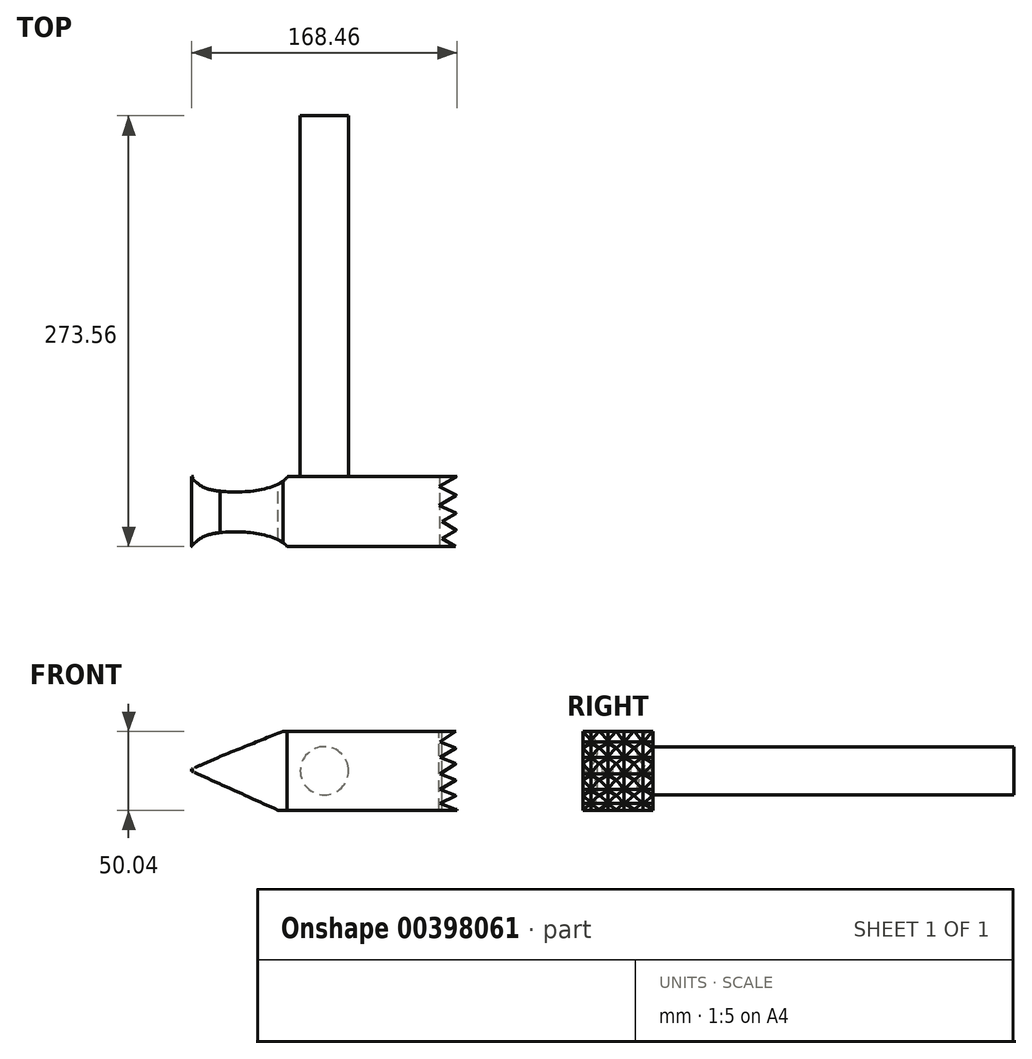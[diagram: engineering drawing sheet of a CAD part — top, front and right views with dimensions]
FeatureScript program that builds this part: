
annotation { "Feature Type Name" : "Feature", "Feature Type Description" : "" }
export const myFeature = defineFeature(function(context is Context, id is Id, definition is map)
    precondition{}
    {
        {
            var Q0;
            Q0=qCreatedBy(makeId("Front.planeOp"),FACE);
            var sketch = newSketch(context, id + "F0", { "sketchPlane" : qUnion([Q0])});
            skCircle(sketch, "E0", {"center": v(0, 0) * mm, "radius": 15.3 * mm});
            skSolve(sketch);
        }
        {
            var Q0;
            Q0 = qSketchRegion(id + "F0", true);
            extrude(context, id + "F1", {"entities" : qUnion([Q0]), "depth" : 229.1 * mm});
        }
        {
            var Q0;
            Q0=makeQuery(id+"F1.opExtrude","CAP_FACE",FACE,{"disambiguationData":[OSD([sQuery(id+"F0.wireOp",EDGE,"E0")])],"isStart":false});
            var sketch = newSketch(context, id + "F2", { "sketchPlane" : qUnion([Q0])});
            skLineSegment(sketch, "E1.bottom", {"start": v(84.23, 25.02) * mm, "end": v(-84.23, 25.02) * mm});
            skLineSegment(sketch, "E1.top", {"start": v(84.23, -25.02) * mm, "end": v(-84.23, -25.02) * mm});
            skLineSegment(sketch, "E1.left", {"start": v(84.23, 25.02) * mm, "end": v(84.23, -25.02) * mm});
            skLineSegment(sketch, "E1.right", {"start": v(-84.23, 25.02) * mm, "end": v(-84.23, -25.02) * mm});
            skPoint(sketch, "E1.middle", {"position": v(0, 0) * mm});
            skSolve(sketch);
        }
        {
            var Q0;
            Q0 = qSketchRegion(id + "F2", true);
            extrude(context, id + "F3", {"entities" : qUnion([Q0]), "operationType" : NewBodyOperationType.ADD, "depth" : 44.45 * mm});
        }
        {
            var Q0;
            Q0=makeQuery(id+"F3.opExtrude","SWEPT_FACE",FACE,{"disambiguationData":[OSD([sQuery(id+"F2.wireOp",EDGE,"E1.bottom")])]});
            cPlane(context, id + "F4", {"entities" : qUnion([Q0]), "cplaneType" : CPlaneType.OFFSET, "offset" : 25.4 * mm, "width" : 152.4 * mm, "height" : 152.4 * mm});
        }
        {
            var Q0;
            Q0=qCreatedBy(id+"F4.planeOp",FACE);
            var sketch = newSketch(context, id + "F5", { "sketchPlane" : qUnion([Q0])});
            skLineSegment(sketch, "E2", {"start": v(83.8, -229.13) * mm, "end": v(72.84, -235.4) * mm});
            skLineSegment(sketch, "E3", {"start": v(72.84, -235.4) * mm, "end": v(83.8, -241.14) * mm});
            skLineSegment(sketch, "E4", {"start": v(83.8, -241.14) * mm, "end": v(72.84, -247.4) * mm});
            skLineSegment(sketch, "E5", {"start": v(72.84, -247.4) * mm, "end": v(83.8, -252.37) * mm});
            skLineSegment(sketch, "E6", {"start": v(83.8, -252.37) * mm, "end": v(74.58, -257.64) * mm});
            skLineSegment(sketch, "E7", {"start": v(74.58, -257.64) * mm, "end": v(83.8, -263.33) * mm});
            skLineSegment(sketch, "E8", {"start": v(83.8, -263.33) * mm, "end": v(74.58, -268.6) * mm});
            skLineSegment(sketch, "E9", {"start": v(74.58, -268.6) * mm, "end": v(83.8, -273.77) * mm});
            skLineSegment(sketch, "E10", {"start": v(83.8, -273.77) * mm, "end": v(99.2, -273.77) * mm});
            skLineSegment(sketch, "E11", {"start": v(99.2, -273.77) * mm, "end": v(99.2, -229.66) * mm});
            skLineSegment(sketch, "E12", {"start": v(99.2, -229.66) * mm, "end": v(83.8, -229.13) * mm});
            skSolve(sketch);
        }
        {
            var Q0;
            Q0 = qSketchRegion(id + "F5", true);
            extrude(context, id + "F6", {"entities" : qUnion([Q0]), "operationType" : NewBodyOperationType.REMOVE, "oppositeDirection" : true, "depth" : 113.8 * mm});
        }
        {
            var Q0;
            Q0=makeQuery(id+"F3.opExtrude","CAP_FACE",FACE,{"disambiguationData":[OSD([sQuery(id+"F2.wireOp",EDGE,"E1.bottom"),sQuery(id+"F2.wireOp",EDGE,"E1.top"),sQuery(id+"F2.wireOp",EDGE,"E1.left"),sQuery(id+"F2.wireOp",EDGE,"E1.right")])],"isStart":true});
            cPlane(context, id + "F7", {"entities" : qUnion([Q0]), "cplaneType" : CPlaneType.OFFSET, "offset" : 25.4 * mm, "width" : 152.4 * mm, "height" : 152.4 * mm});
        }
        {
            var Q0;
            Q0=qCreatedBy(id+"F7.planeOp",FACE);
            var sketch = newSketch(context, id + "F8", { "sketchPlane" : qUnion([Q0])});
            skLineSegment(sketch, "E13", {"start": v(-83.88, 25.3) * mm, "end": v(-73.3, 18.32) * mm});
            skLineSegment(sketch, "E14", {"start": v(-73.3, 18.32) * mm, "end": v(-83.62, 14.45) * mm});
            skLineSegment(sketch, "E15", {"start": v(-83.62, 14.45) * mm, "end": v(-73.3, 8.52) * mm});
            skLineSegment(sketch, "E16", {"start": v(-73.3, 8.52) * mm, "end": v(-83.62, 4.65) * mm});
            skLineSegment(sketch, "E17", {"start": v(-83.62, 4.65) * mm, "end": v(-73.3, -2.06) * mm});
            skLineSegment(sketch, "E18", {"start": v(-73.3, -2.06) * mm, "end": v(-83.62, -5.94) * mm});
            skLineSegment(sketch, "E19", {"start": v(-83.62, -5.94) * mm, "end": v(-73.3, -11.87) * mm});
            skLineSegment(sketch, "E20", {"start": v(-73.3, -11.87) * mm, "end": v(-83.62, -15.74) * mm});
            skLineSegment(sketch, "E21", {"start": v(-83.62, -15.74) * mm, "end": v(-73.3, -20.65) * mm});
            skLineSegment(sketch, "E22", {"start": v(-73.3, -20.65) * mm, "end": v(-83.62, -24.52) * mm});
            skLineSegment(sketch, "E23", {"start": v(-83.62, -24.52) * mm, "end": v(-96.01, -24.52) * mm});
            skLineSegment(sketch, "E24", {"start": v(-96.01, -24.52) * mm, "end": v(-96.01, 27.87) * mm});
            skLineSegment(sketch, "E25", {"start": v(-96.01, 27.87) * mm, "end": v(-83.88, 25.3) * mm});
            skSolve(sketch);
        }
        {
            var Q0;
            Q0 = qSketchRegion(id + "F8", true);
            extrude(context, id + "F9", {"entities" : qUnion([Q0]), "operationType" : NewBodyOperationType.REMOVE, "oppositeDirection" : true, "depth" : 115.57 * mm});
        }
        {
            var Q0;
            Q0=makeQuery(id+"F3.opExtrude","SWEPT_FACE",FACE,{"disambiguationData":[OSD([sQuery(id+"F2.wireOp",EDGE,"E1.top")])]});
            cPlane(context, id + "F10", {"entities" : qUnion([Q0]), "cplaneType" : CPlaneType.OFFSET, "offset" : 25.4 * mm, "width" : 152.4 * mm, "height" : 152.4 * mm});
        }
        {
            var Q0;
            Q0=qCreatedBy(id+"F10.planeOp",FACE);
            var sketch = newSketch(context, id + "F11", { "sketchPlane" : qUnion([Q0])});
            skFitSpline(sketch, "E26", {"points": [v(-84.27, 273.35) * mm, v(-75.33, 266.78) * mm, v(-54.16, 264.4) * mm, v(-37, 266.6) * mm, v(-23.31, 274.26) * mm, v(-27.33, 282.1) * mm, v(-71.86, 282.47) * mm, v(-71.5, 283.2) * mm], "startDerivative": vector(58.95, -60.06) * mm, "endDerivative": vector(26.95, 24.73) * mm});
            skFitSpline(sketch, "E27", {"points": [v(-71.5, 283.2) * mm, v(-84.27, 273.35) * mm], "startDerivative": vector(-12.78, -9.86) * mm, "endDerivative": vector(-12.78, -9.86) * mm});
            skLineSegment(sketch, "E28", {"start": v(-84.77, 251.68) * mm, "end": v(-18.13, 251.68) * mm, "construction": true});
            skFitSpline(sketch, "E29.MirrorCS", {"points": [v(-84.27, 230.01) * mm, v(-75.33, 236.58) * mm, v(-54.16, 238.95) * mm, v(-37, 236.76) * mm, v(-23.31, 229.1) * mm, v(-27.33, 221.25) * mm, v(-71.86, 220.89) * mm, v(-71.5, 220.16) * mm], "startDerivative": vector(58.95, 60.06) * mm, "endDerivative": vector(26.95, -24.73) * mm});
            skLineSegment(sketch, "E30", {"start": v(-71.5, 220.16) * mm, "end": v(-84.27, 230.01) * mm});
            skSolve(sketch);
        }
        {
            var Q0;
            Q0 = qSketchRegion(id + "F11", true);
            extrude(context, id + "F12", {"entities" : qUnion([Q0]), "operationType" : NewBodyOperationType.REMOVE, "oppositeDirection" : true, "depth" : 134.11 * mm});
        }
        {
            var Q0;
            Q0=qCreatedBy(id+"F7.planeOp",FACE);
            var sketch = newSketch(context, id + "F13", { "sketchPlane" : qUnion([Q0])});
            skLineSegment(sketch, "E31", {"start": v(84.38, 1.77) * mm, "end": v(22.53, 26.57) * mm});
            skLineSegment(sketch, "E32", {"start": v(22.53, 26.57) * mm, "end": v(88.52, 26.57) * mm});
            skLineSegment(sketch, "E33", {"start": v(88.52, 26.57) * mm, "end": v(90.84, -27.03) * mm});
            skLineSegment(sketch, "E34", {"start": v(90.84, -27.03) * mm, "end": v(18, -30.19) * mm});
            skLineSegment(sketch, "E35", {"start": v(18, -30.19) * mm, "end": v(84.9, 0) * mm});
            skLineSegment(sketch, "E36", {"start": v(84.9, 0) * mm, "end": v(84.38, 1.77) * mm});
            skSolve(sketch);
        }
        {
            var Q0;
            Q0 = qSketchRegion(id + "F13", true);
            extrude(context, id + "F14", {"entities" : qUnion([Q0]), "operationType" : NewBodyOperationType.REMOVE, "oppositeDirection" : true, "depth" : 79.5 * mm});
        }
        {
            var Q0;
            Q0=qCreatedBy(makeId("Front.planeOp"),FACE);
            cPlane(context, id + "F15", {"entities" : qUnion([Q0]), "cplaneType" : CPlaneType.OFFSET, "offset" : 312.67 * mm, "width" : 152.4 * mm, "height" : 152.4 * mm});
        }
        {
            var Q0;
            Q0=qCreatedBy(id+"F15.planeOp",FACE);
            var sketch = newSketch(context, id + "F16", { "sketchPlane" : qUnion([Q0])});
            skLineSegment(sketch, "E37", {"start": v(-86.63, 0) * mm, "end": v(-27.1, 26.4) * mm});
            skLineSegment(sketch, "E38", {"start": v(-27.1, 26.4) * mm, "end": v(-27.1, 38.92) * mm});
            skLineSegment(sketch, "E39", {"start": v(-27.1, 38.92) * mm, "end": v(-110.96, 38.92) * mm});
            skLineSegment(sketch, "E40", {"start": v(-110.96, 38.92) * mm, "end": v(-110.96, 0) * mm});
            skLineSegment(sketch, "E41", {"start": v(-110.96, 0) * mm, "end": v(-110.96, -39.15) * mm});
            skLineSegment(sketch, "E42", {"start": v(-110.96, -39.15) * mm, "end": v(-27.1, -39.15) * mm});
            skLineSegment(sketch, "E43", {"start": v(-27.1, -39.15) * mm, "end": v(-27.1, -28.03) * mm});
            skLineSegment(sketch, "E44", {"start": v(-27.1, -28.03) * mm, "end": v(-86.63, 0) * mm});
            skSolve(sketch);
        }
        {
            var Q0;
            Q0 = qSketchRegion(id + "F16", true);
            extrude(context, id + "F17", {"entities" : qUnion([Q0]), "operationType" : NewBodyOperationType.REMOVE, "oppositeDirection" : true, "depth" : 139.95 * mm});
        }
    });
